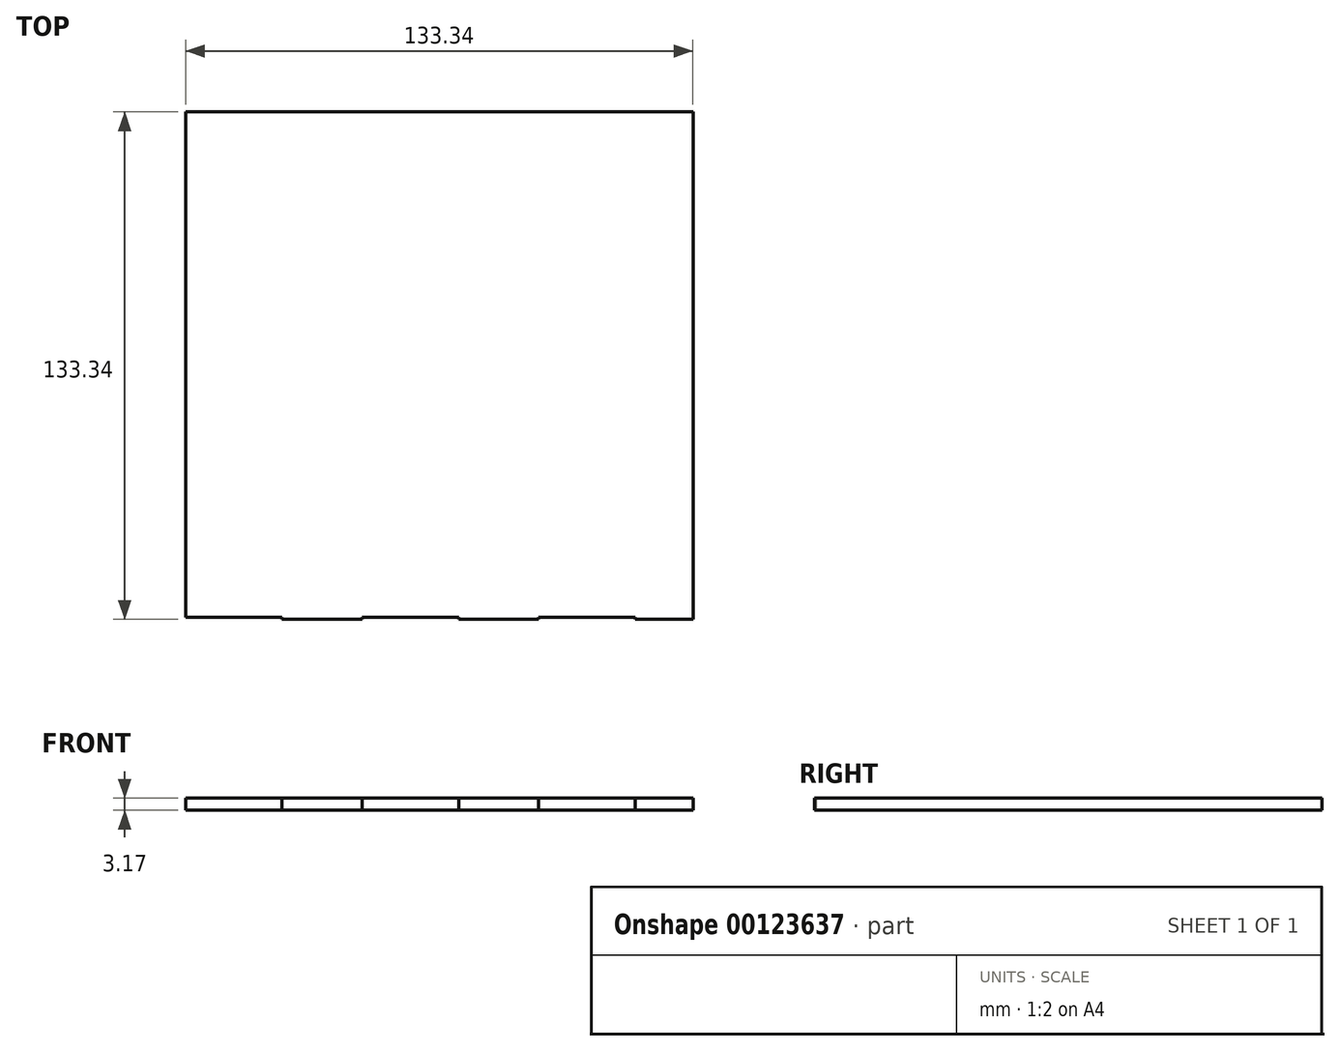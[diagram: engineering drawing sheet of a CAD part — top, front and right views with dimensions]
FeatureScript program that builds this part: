
annotation { "Feature Type Name" : "Feature", "Feature Type Description" : "" }
export const myFeature = defineFeature(function(context is Context, id is Id, definition is map)
    precondition{}
    {
        {
            var Q0;
            Q0=qCreatedBy(makeId("Top.planeOp"),FACE);
            var sketch = newSketch(context, id + "F0", { "sketchPlane" : qUnion([Q0])});
            skLineSegment(sketch, "E0.bottom", {"start": v(66.68, 66.68) * mm, "end": v(-66.68, 66.68) * mm});
            skLineSegment(sketch, "E0.top", {"start": v(66.68, -66.68) * mm, "end": v(-66.68, -66.68) * mm});
            skLineSegment(sketch, "E0.left", {"start": v(66.68, 66.68) * mm, "end": v(66.68, -66.68) * mm});
            skLineSegment(sketch, "E0.right", {"start": v(-66.68, 66.67) * mm, "end": v(-66.68, -66.68) * mm});
            skPoint(sketch, "E0.middle", {"position": v(0, 0) * mm});
            skSolve(sketch);
        }
        {
            var Q0;
            Q0=makeQuery(id+"F0.imprint","IMPRINT",FACE,{"disambiguationData":[TD([[makeQuery(id+"F0.imprint","IMPRINT",EDGE,{"derivedFrom":sQuery(id+"F0.wireOp",EDGE,"E0.bottom")}),1.0]])]});
            extrude(context, id + "F1", {"entities" : qUnion([Q0]), "depth" : 3.17 * mm});
        }
        {
            var Q0;
            Q0=qCreatedBy(makeId("Top.planeOp"),FACE);
            var sketch = newSketch(context, id + "F2", { "sketchPlane" : qUnion([Q0])});
            skLineSegment(sketch, "E1.bottom", {"start": v(-66.68, -66.68) * mm, "end": v(66.68, -66.68) * mm});
            skLineSegment(sketch, "E1.top", {"start": v(-66.68, -63.5) * mm, "end": v(66.68, -63.5) * mm});
            skLineSegment(sketch, "E1.left", {"start": v(-66.68, -66.68) * mm, "end": v(-66.68, -63.5) * mm});
            skLineSegment(sketch, "E1.right", {"start": v(66.68, -66.68) * mm, "end": v(66.68, -63.5) * mm});
            skSolve(sketch);
        }
        {
            var Q0;
            Q0=sQuery(id+"F2.wireOp",EDGE,"E1.bottom");
            var Q1;
            Q1=sQuery(id+"F2.wireOp",EDGE,"E1.left");
            var Q2;
            Q2=sQuery(id+"F2.wireOp",EDGE,"E1.right");
            extrude(context, id + "F3", {"bodyType" : ToolBodyType.SURFACE, "surfaceEntities" : qUnion([Q0, Q1, Q2]), "depth" : 127 * mm});
        }
        {
            var Q0;
            Q0=makeQuery(id+"F3.opExtrude","SWEPT_FACE",FACE,{"disambiguationData":[OSD([sQuery(id+"F2.wireOp",EDGE,"E1.bottom")])]});
            var sketch = newSketch(context, id + "F4", { "sketchPlane" : qUnion([Q0])});
            skLineSegment(sketch, "E2.bottom", {"start": v(-66.68, 3.33) * mm, "end": v(-41.28, 3.33) * mm});
            skLineSegment(sketch, "E2.top", {"start": v(-66.68, 0) * mm, "end": v(-41.28, 0) * mm});
            skLineSegment(sketch, "E2.left", {"start": v(-66.68, 3.33) * mm, "end": v(-66.68, 0) * mm});
            skLineSegment(sketch, "E2.right", {"start": v(-41.28, 3.33) * mm, "end": v(-41.28, 0) * mm});
            skLineSegment(sketch, "E3.bottom", {"start": v(-20.32, 3.33) * mm, "end": v(5.08, 3.33) * mm});
            skLineSegment(sketch, "E3.top", {"start": v(-20.32, 0) * mm, "end": v(5.08, 0) * mm});
            skLineSegment(sketch, "E3.left", {"start": v(-20.32, 3.33) * mm, "end": v(-20.32, 0) * mm});
            skLineSegment(sketch, "E3.right", {"start": v(5.08, 3.33) * mm, "end": v(5.08, 0) * mm});
            skLineSegment(sketch, "E4.bottom", {"start": v(26.03, 3.33) * mm, "end": v(51.43, 3.33) * mm});
            skLineSegment(sketch, "E4.top", {"start": v(26.03, 0) * mm, "end": v(51.43, 0) * mm});
            skLineSegment(sketch, "E4.left", {"start": v(26.03, 3.33) * mm, "end": v(26.03, 0) * mm});
            skLineSegment(sketch, "E4.right", {"start": v(51.43, 3.33) * mm, "end": v(51.43, 0) * mm});
            skSolve(sketch);
        }
        {
            var Q0;
            Q0=makeQuery(id+"F4.imprint","IMPRINT",FACE,{"disambiguationData":[TD([[makeQuery(id+"F4.imprint","IMPRINT",EDGE,{"derivedFrom":sQuery(id+"F4.wireOp",EDGE,"E2.bottom")}),-1.0]])]});
            var Q1;
            Q1=makeQuery(id+"F4.imprint","IMPRINT",FACE,{"disambiguationData":[TD([[makeQuery(id+"F4.imprint","IMPRINT",EDGE,{"derivedFrom":sQuery(id+"F4.wireOp",EDGE,"E3.bottom")}),-1.0]])]});
            var Q2;
            Q2=makeQuery(id+"F4.imprint","IMPRINT",FACE,{"disambiguationData":[TD([[makeQuery(id+"F4.imprint","IMPRINT",EDGE,{"derivedFrom":sQuery(id+"F4.wireOp",EDGE,"E4.bottom")}),-1.0]])]});
            extrude(context, id + "F5", {"entities" : qUnion([Q0, Q1, Q2]), "operationType" : NewBodyOperationType.REMOVE, "oppositeDirection" : true, "depth" : 0.5 * mm});
        }
    });
